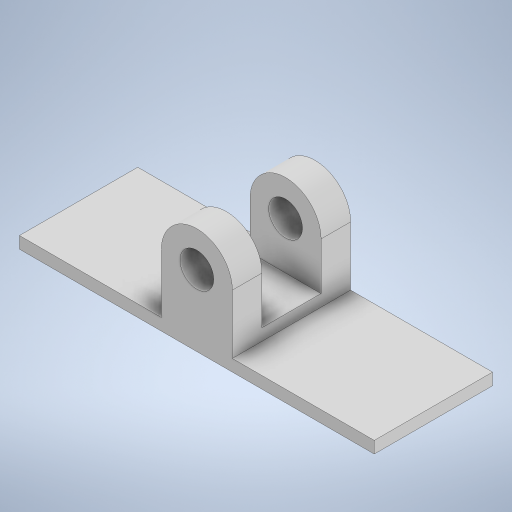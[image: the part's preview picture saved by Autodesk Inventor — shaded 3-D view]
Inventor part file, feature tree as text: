
AUTODESK INVENTOR PART (.ipt)
format: ipt  version: 2023 (Build 270158000, 158)  size: 277,504 bytes
history: native  units: mm
features: extrude x4, sketch x4
ambient origin geometry x8: Origin, YZ Plane, XZ Plane, XY Plane, X Axis, Y Axis, Z Axis, Center Point
bodies: Solid1 (feature_tree)
feature tree (8):
  extrude  "Extrusion1"  Depth=30.0mm
  extrude  "Extrusion2"  Depth=1.0mm
  extrude  "Extrusion4"  Depth=2.5mm TaperAngle=0.0deg
  extrude  "Extrusion5"  Depth=2.5mm
  sketch  "Sketch1"  dims[d0=10.0mm d1=30.0mm]
  sketch  "Sketch2"  dims[d2=1.0mm d3=0.0mm d4=15.0mm]
  sketch  "Sketch4"  dims[d5=2.5mm d9=8.0mm d10=0.0mm]
  sketch  "Sketch5"  dims[d20=3.0mm d21=2.5mm d22=6.0mm d23=2.5mm d24=3.0mm d25=2.5mm d26=6.0mm d27=3.0mm d28=2.85mm d29=0.0mm d30=0.0mm d31=1.0mm d32=0.0mm]
